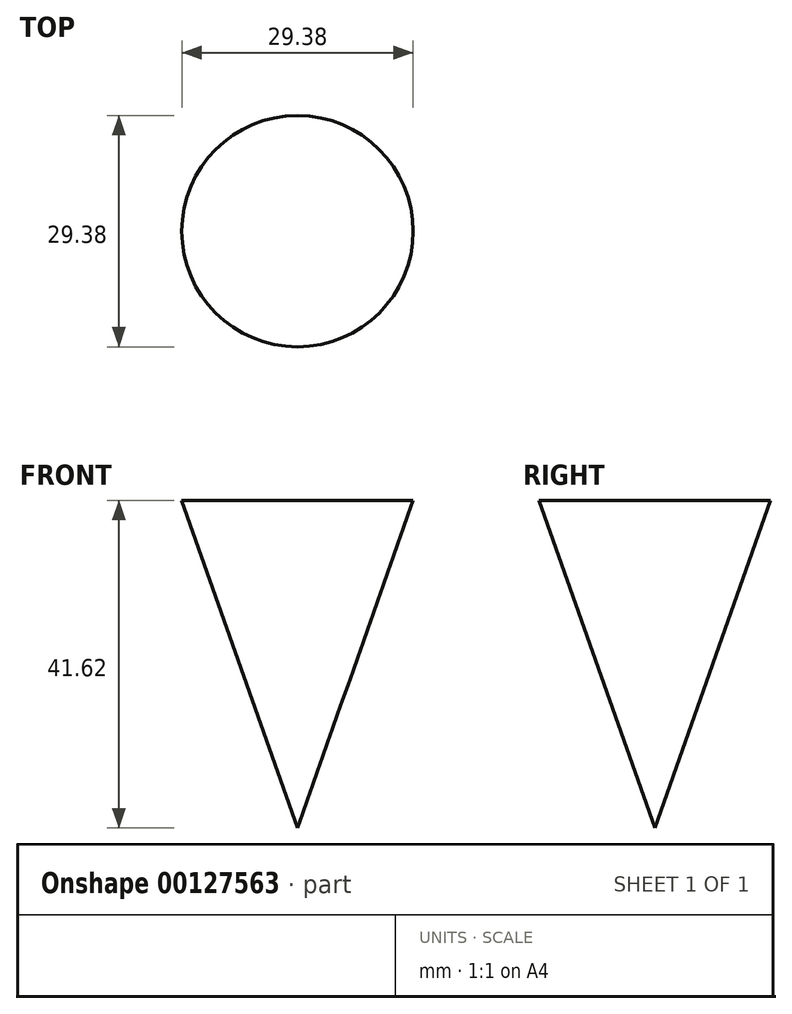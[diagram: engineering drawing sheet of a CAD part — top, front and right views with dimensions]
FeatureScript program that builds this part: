
annotation { "Feature Type Name" : "Feature", "Feature Type Description" : "" }
export const myFeature = defineFeature(function(context is Context, id is Id, definition is map)
    precondition{}
    {
        {
            var Q0;
            Q0=qCreatedBy(makeId("Front.planeOp"),FACE);
            var sketch = newSketch(context, id + "F0", { "sketchPlane" : qUnion([Q0])});
            skLineSegment(sketch, "E0", {"start": v(0, 41.62) * mm, "end": v(0, -85.38) * mm});
            skLineSegment(sketch, "E1", {"start": v(0, 41.62) * mm, "end": v(-76.2, 41.62) * mm});
            skLineSegment(sketch, "E2", {"start": v(-76.2, 41.62) * mm, "end": v(-76.2, -85.38) * mm});
            skLineSegment(sketch, "E3", {"start": v(-76.2, -85.38) * mm, "end": v(0, -85.38) * mm});
            skLineSegment(sketch, "E4", {"start": v(-14.7, 41.62) * mm, "end": v(0, 0) * mm});
            skLineSegment(sketch, "E5", {"start": v(-66.58, 41.62) * mm, "end": v(-46.95, 0) * mm});
            skLineSegment(sketch, "E6", {"start": v(-32.85, 41.62) * mm, "end": v(-46.95, 0) * mm});
            skLineSegment(sketch, "E7", {"start": v(-66.58, 41.62) * mm, "end": v(-32.85, 41.62) * mm});
            skLineSegment(sketch, "E8", {"start": v(-14.7, 41.62) * mm, "end": v(0, 41.62) * mm});
            skLineSegment(sketch, "E9", {"start": v(0, 41.62) * mm, "end": v(0, 0) * mm});
            skLineSegment(sketch, "E10", {"start": v(-32.85, 41.62) * mm, "end": v(-14.7, 41.62) * mm});
            skSolve(sketch);
        }
        {
            var Q0;
            Q0=makeQuery(id+"F0.imprint","IMPRINT",FACE,{"disambiguationData":[TD([[makeQuery(id+"F0.imprint","IMPRINT",EDGE,{"derivedFrom":sQuery(id+"F0.wireOp",EDGE,"E0")}),-1.0]])]});
            var Q1;
            Q1=sQuery(id+"F0.wireOp",EDGE,"E0");
            revolve(context, id + "F1", {"entities" : qUnion([Q0]), "axis" : qUnion([Q1]), "revolveType" : RevolveType.FULL});
        }
    });
